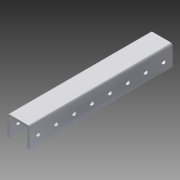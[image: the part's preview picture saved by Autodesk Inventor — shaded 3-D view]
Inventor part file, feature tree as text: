
AUTODESK INVENTOR PART (.ipt)
format: ipt  version: 2015 SP1 (Build 190203100, 203)  size: 148,480 bytes
history: native  units: in
note: dims shown in document units (in); Inventor stores cm internally (conversion verified against a paired STEP export)
features: extrude x2, sketch x2, pattern_linear x1
ambient origin geometry x8: Origin, YZ Plane, XZ Plane, XY Plane, X Axis, Y Axis, Z Axis, Center Point
bodies: Solid1 (feature_tree)
feature tree (5):
  extrude  "Extrusion1"  Depth=8.0in
  extrude  "Extrusion4"  Depth=1.0in
  pattern_linear  "Rectangular Pattern3"  Spacing1=0.5in  [1 undecoded]
  sketch  "Sketch1"  dims[d0=1.13in d1=1.25in d2=0.125in d3=0.125in d4=0.125in d5=8.0in]
  sketch  "Sketch4"  dims[d6=0.0in d34=0.25in d35=0.5in d36=0.5in d37=1.0in d38=0.0in d39=3.937in d41=1.0in d42=3.937in d44=1.0in]
note: 1 required parameter value undecoded (feature->parameter linkage not recoverable at this tier; creation-order binding heuristic only, values carry confidence <= 0.55)
